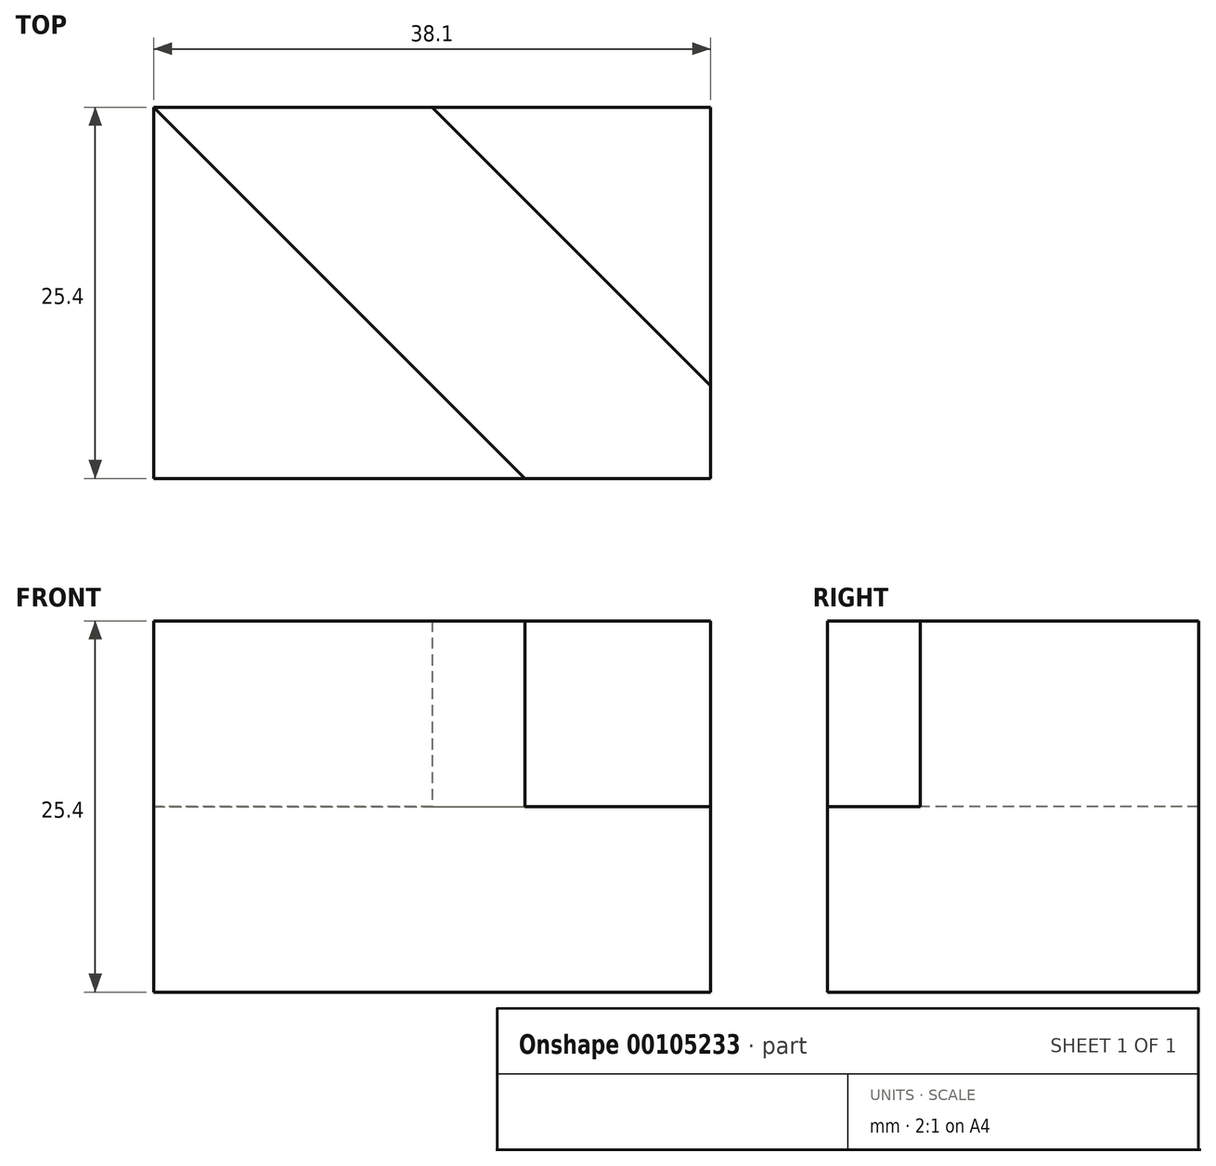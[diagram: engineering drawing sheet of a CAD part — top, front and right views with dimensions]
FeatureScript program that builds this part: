
annotation { "Feature Type Name" : "Feature", "Feature Type Description" : "" }
export const myFeature = defineFeature(function(context is Context, id is Id, definition is map)
    precondition{}
    {
        {
            var Q0;
            Q0=qCreatedBy(makeId("Front.planeOp"),FACE);
            var sketch = newSketch(context, id + "F0", { "sketchPlane" : qUnion([Q0])});
            skLineSegment(sketch, "E0.bottom", {"start": v(0, 0) * mm, "end": v(-38.1, 0) * mm});
            skLineSegment(sketch, "E0.top", {"start": v(0, 25.4) * mm, "end": v(-38.1, 25.4) * mm});
            skLineSegment(sketch, "E0.left", {"start": v(0, 0) * mm, "end": v(0, 25.4) * mm});
            skLineSegment(sketch, "E0.right", {"start": v(-38.1, 0) * mm, "end": v(-38.1, 25.4) * mm});
            skSolve(sketch);
        }
        {
            var Q0;
            Q0 = qSketchRegion(id + "F0", true);
            extrude(context, id + "F1", {"entities" : qUnion([Q0]), "endBound" : BoundingType.SYMMETRIC, "oppositeDirection" : true, "depth" : 25.4 * mm});
        }
        {
            var Q0;
            Q0=qCreatedBy(makeId("Top.planeOp"),FACE);
            var sketch = newSketch(context, id + "F2", { "sketchPlane" : qUnion([Q0])});
            skLineSegment(sketch, "E1", {"start": v(-38.1, 12.7) * mm, "end": v(-12.7, -12.7) * mm});
            skLineSegment(sketch, "E2", {"start": v(-38.1, 12.7) * mm, "end": v(-19.05, 12.7) * mm});
            skLineSegment(sketch, "E3", {"start": v(-19.05, 12.7) * mm, "end": v(0, -6.35) * mm});
            skLineSegment(sketch, "E4", {"start": v(0, -6.35) * mm, "end": v(0, -12.7) * mm});
            skLineSegment(sketch, "E5", {"start": v(0, -12.7) * mm, "end": v(-12.7, -12.7) * mm});
            skSolve(sketch);
        }
        {
            var Q0;
            Q0 = qSketchRegion(id + "F2", true);
            extrude(context, id + "F3", {"entities" : qUnion([Q0]), "operationType" : NewBodyOperationType.REMOVE, "depth" : 25.4 * mm});
        }
        {
            var Q0;
            Q0=qCreatedBy(makeId("Front.planeOp"),FACE);
            var sketch = newSketch(context, id + "F4", { "sketchPlane" : qUnion([Q0])});
            skLineSegment(sketch, "E6.bottom", {"start": v(0, 0) * mm, "end": v(-38.1, 0) * mm});
            skLineSegment(sketch, "E6.top", {"start": v(0, 12.7) * mm, "end": v(-38.1, 12.7) * mm});
            skLineSegment(sketch, "E6.left", {"start": v(0, 0) * mm, "end": v(0, 12.7) * mm});
            skLineSegment(sketch, "E6.right", {"start": v(-38.1, 0) * mm, "end": v(-38.1, 12.7) * mm});
            skSolve(sketch);
        }
        {
            var Q0;
            Q0 = qSketchRegion(id + "F4", true);
            extrude(context, id + "F5", {"entities" : qUnion([Q0]), "operationType" : NewBodyOperationType.ADD, "oppositeDirection" : true, "depth" : 12.7 * mm, "hasSecondDirection" : true, "secondDirectionOppositeDirection" : false, "secondDirectionDepth" : 12.7 * mm});
        }
    });
